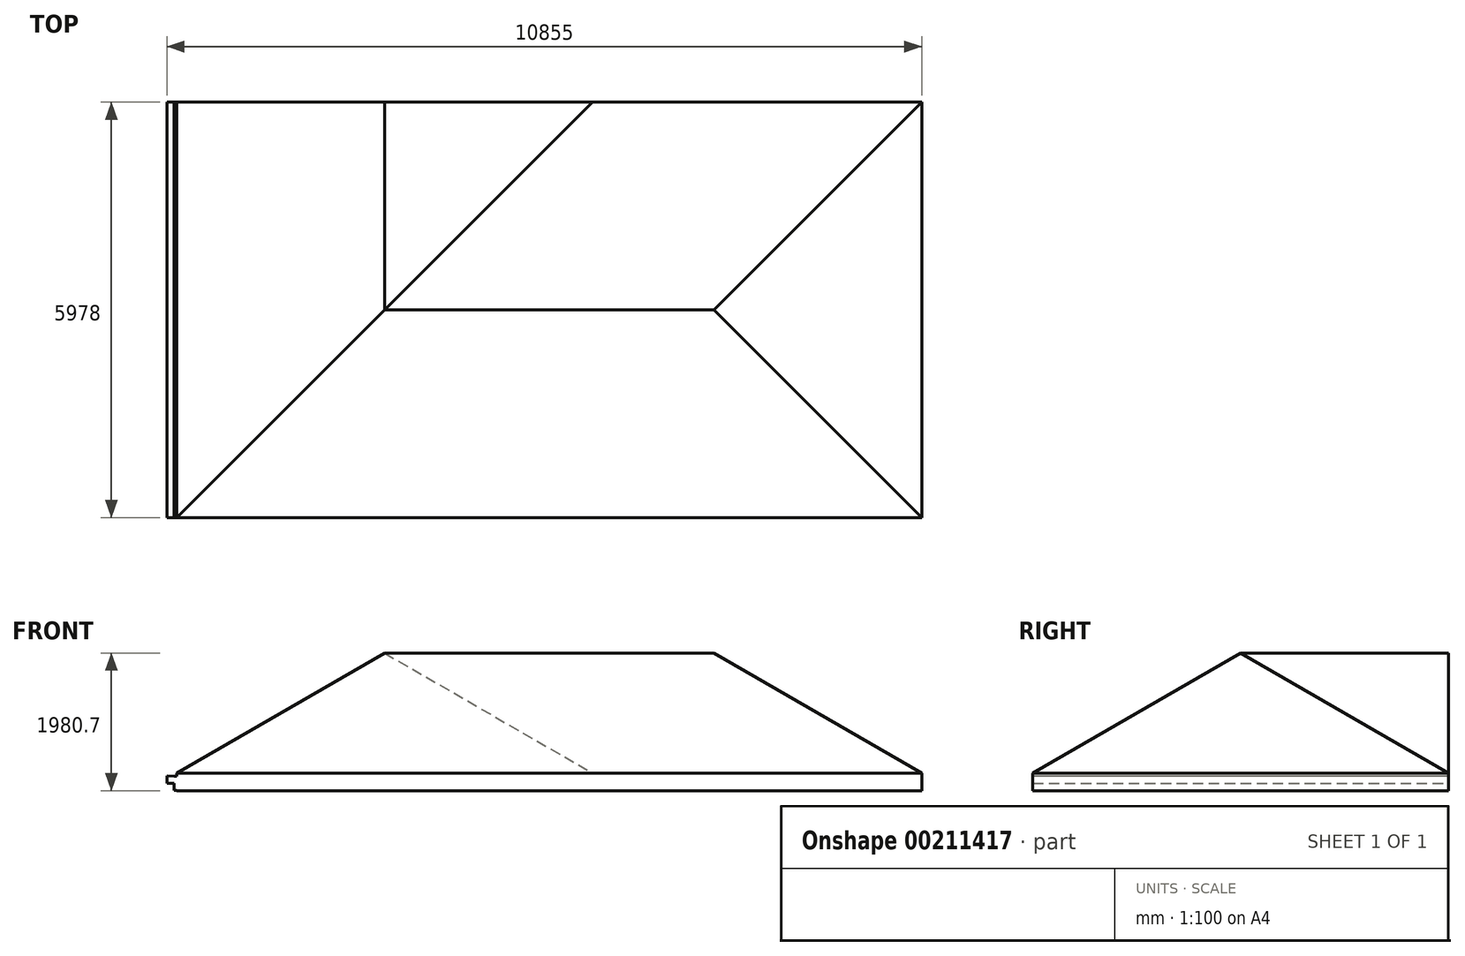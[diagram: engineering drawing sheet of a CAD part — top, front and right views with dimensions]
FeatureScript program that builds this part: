
annotation { "Feature Type Name" : "Feature", "Feature Type Description" : "" }
export const myFeature = defineFeature(function(context is Context, id is Id, definition is map)
    precondition{}
    {
        {
            var Q0;
            Q0=qCreatedBy(makeId("Right.planeOp"),FACE);
            var sketch = newSketch(context, id + "F0", { "sketchPlane" : qUnion([Q0])});
            skLineSegment(sketch, "E0", {"start": v(0, 0) * mm, "end": v(0, 255) * mm});
            skLineSegment(sketch, "E1", {"start": v(0, 255) * mm, "end": v(2989, 1980.7) * mm});
            skLineSegment(sketch, "E2", {"start": v(2989, 1980.7) * mm, "end": v(5978, 255) * mm});
            skLineSegment(sketch, "E3", {"start": v(5978, 255) * mm, "end": v(5978, 0) * mm});
            skLineSegment(sketch, "E4", {"start": v(5978, 0) * mm, "end": v(0, 0) * mm});
            skLineSegment(sketch, "E5", {"start": v(2989, 1980.7) * mm, "end": v(2989, 0) * mm, "construction": true});
            skSolve(sketch);
        }
        {
            var Q0;
            Q0=makeQuery(id+"F0.imprint","IMPRINT",FACE,{"disambiguationData":[TD([[makeQuery(id+"F0.imprint","IMPRINT",EDGE,{"derivedFrom":sQuery(id+"F0.wireOp",EDGE,"E0")}),-1.0]])]});
            extrude(context, id + "F1", {"entities" : qUnion([Q0]), "depth" : 10715 * mm});
        }
        {
            var Q0;
            Q0=qCreatedBy(makeId("Front.planeOp"),FACE);
            var sketch = newSketch(context, id + "F2", { "sketchPlane" : qUnion([Q0])});
            skLineSegment(sketch, "E6", {"start": v(0, 255) * mm, "end": v(0, 1980.7) * mm});
            skLineSegment(sketch, "E7", {"start": v(0, 1980.7) * mm, "end": v(2989, 1980.7) * mm});
            skLineSegment(sketch, "E8", {"start": v(2989, 1980.7) * mm, "end": v(0, 255) * mm});
            skLineSegment(sketch, "E9", {"start": v(10715, 255) * mm, "end": v(10715, 1980.7) * mm});
            skLineSegment(sketch, "E10", {"start": v(10715, 1980.7) * mm, "end": v(7726, 1980.7) * mm});
            skLineSegment(sketch, "E11", {"start": v(7726, 1980.7) * mm, "end": v(10715, 255) * mm});
            skSolve(sketch);
        }
        {
            var Q0;
            Q0=makeQuery(id+"F2.imprint","IMPRINT",FACE,{"disambiguationData":[TD([[makeQuery(id+"F2.imprint","IMPRINT",EDGE,{"derivedFrom":sQuery(id+"F2.wireOp",EDGE,"E6")}),-1.0]])]});
            var Q1;
            Q1=makeQuery(id+"F2.imprint","IMPRINT",FACE,{"disambiguationData":[TD([[makeQuery(id+"F2.imprint","IMPRINT",EDGE,{"derivedFrom":sQuery(id+"F2.wireOp",EDGE,"E9")}),1.0]])]});
            extrude(context, id + "F3", {"entities" : qUnion([Q0, Q1]), "operationType" : NewBodyOperationType.REMOVE, "endBound" : BoundingType.THROUGH_ALL, "oppositeDirection" : true, "depth" : 25 * mm});
        }
        {
            var Q0;
            Q0=makeQuery(id+"F1.opExtrude","SWEPT_FACE",FACE,{"disambiguationData":[OSD([sQuery(id+"F0.wireOp",EDGE,"E3")])]});
            var sketch = newSketch(context, id + "F4", { "sketchPlane" : qUnion([Q0])});
            skLineSegment(sketch, "E12", {"start": v(0, 255) * mm, "end": v(-5978, 255) * mm});
            skLineSegment(sketch, "E13", {"start": v(-5978, 255) * mm, "end": v(-2989, 1980.7) * mm});
            skLineSegment(sketch, "E14", {"start": v(-2989, 1980.7) * mm, "end": v(0, 255) * mm});
            skSolve(sketch);
        }
        {
            var Q0;
            Q0=makeQuery(id+"F4.imprint","IMPRINT",FACE,{"disambiguationData":[TD([[makeQuery(id+"F4.imprint","IMPRINT",EDGE,{"derivedFrom":sQuery(id+"F4.wireOp",EDGE,"E12")}),1.0]])]});
            var Q1;
            Q1=makeQuery(id+"F1.opExtrude","SWEPT_FACE",FACE,{"disambiguationData":[OSD([sQuery(id+"F0.wireOp",EDGE,"E2")])]});
            extrude(context, id + "F5", {"entities" : qUnion([Q0]), "operationType" : NewBodyOperationType.ADD, "endBound" : BoundingType.UP_TO_SURFACE, "oppositeDirection" : true, "endBoundEntityFace" : qUnion([Q1]), "depth" : 25 * mm});
        }
        {
            var Q0;
            Q0=makeQuery(id+"F1.opExtrude","CAP_FACE",FACE,{"disambiguationData":[OSD([sQuery(id+"F0.wireOp",EDGE,"E0"),sQuery(id+"F0.wireOp",EDGE,"E1"),sQuery(id+"F0.wireOp",EDGE,"E2"),sQuery(id+"F0.wireOp",EDGE,"E3"),sQuery(id+"F0.wireOp",EDGE,"E4")])],"isStart":true});
            var sketch = newSketch(context, id + "F6", { "sketchPlane" : qUnion([Q0])});
            skLineSegment(sketch, "E15.bottom", {"start": v(-5978, 5) * mm, "end": v(0, 5) * mm});
            skLineSegment(sketch, "E15.top", {"start": v(-5978, 205) * mm, "end": v(0, 205) * mm});
            skLineSegment(sketch, "E15.left", {"start": v(-5978, 5) * mm, "end": v(-5978, 205) * mm});
            skLineSegment(sketch, "E15.right", {"start": v(0, 5) * mm, "end": v(0, 205) * mm});
            skSolve(sketch);
        }
        {
            var Q0;
            Q0=makeQuery(id+"F6.imprint","IMPRINT",FACE,{"disambiguationData":[TD([[makeQuery(id+"F6.imprint","IMPRINT",EDGE,{"derivedFrom":sQuery(id+"F6.wireOp",EDGE,"E15.bottom")}),1.0]])]});
            extrude(context, id + "F7", {"entities" : qUnion([Q0]), "operationType" : NewBodyOperationType.ADD, "depth" : 40 * mm});
        }
        {
            var Q0;
            Q0=makeQuery(id+"F7.boolean.opBoolean","MERGE",FACE,{"derivedFrom":[makeQuery(id+"F5.boolean.opBoolean","MERGE",FACE,{"derivedFrom":[makeQuery(id+"F1.opExtrude","SWEPT_FACE",FACE,{"disambiguationData":[OSD([sQuery(id+"F0.wireOp",EDGE,"E3")])]}),makeQuery(id+"F5.opExtrude","CAP_FACE",FACE,{"disambiguationData":[OSD([sQuery(id+"F4.wireOp",EDGE,"E12"),sQuery(id+"F4.wireOp",EDGE,"E13"),sQuery(id+"F4.wireOp",EDGE,"E14")])],"isStart":true})]}),makeQuery(id+"F7.opExtrude","SWEPT_FACE",FACE,{"disambiguationData":[OSD([sQuery(id+"F6.wireOp",EDGE,"E15.left")])]})]});
            var sketch = newSketch(context, id + "F8", { "sketchPlane" : qUnion([Q0])});
            skLineSegment(sketch, "E16", {"start": v(40, 205) * mm, "end": v(40, 105) * mm});
            skLineSegment(sketch, "E17", {"start": v(40, 105) * mm, "end": v(140, 105) * mm});
            skLineSegment(sketch, "E18", {"start": v(140, 105) * mm, "end": v(140, 215) * mm});
            skLineSegment(sketch, "E19", {"start": v(40, 205) * mm, "end": v(140, 215) * mm});
            skSolve(sketch);
        }
        {
            var Q0;
            Q0=makeQuery(id+"F8.imprint","IMPRINT",FACE,{"disambiguationData":[TD([[makeQuery(id+"F8.imprint","IMPRINT",EDGE,{"derivedFrom":sQuery(id+"F8.wireOp",EDGE,"E16")}),1.0]])]});
            var Q1;
            Q1=makeQuery(id+"F7.boolean.opBoolean","MERGE",FACE,{"derivedFrom":[makeQuery(id+"F1.opExtrude","SWEPT_FACE",FACE,{"disambiguationData":[OSD([sQuery(id+"F0.wireOp",EDGE,"E0")])]}),makeQuery(id+"F7.opExtrude","SWEPT_FACE",FACE,{"disambiguationData":[OSD([sQuery(id+"F6.wireOp",EDGE,"E15.right")])]})]});
            extrude(context, id + "F9", {"entities" : qUnion([Q0]), "operationType" : NewBodyOperationType.ADD, "endBound" : BoundingType.UP_TO_SURFACE, "oppositeDirection" : true, "endBoundEntityFace" : qUnion([Q1]), "depth" : 25 * mm});
        }
    });
